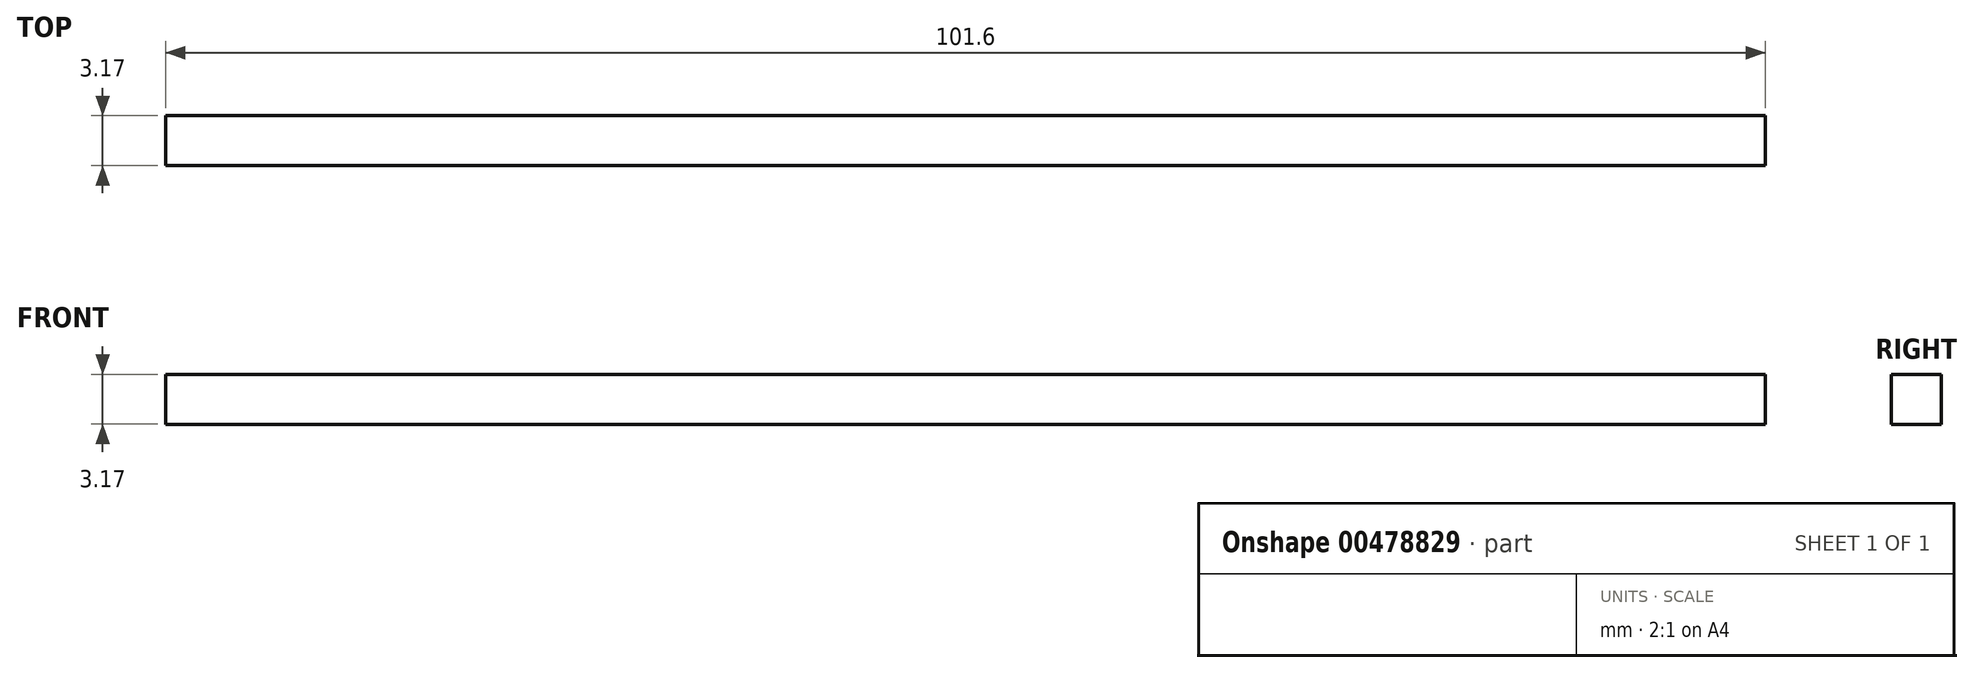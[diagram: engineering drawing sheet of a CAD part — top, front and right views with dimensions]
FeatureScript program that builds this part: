
annotation { "Feature Type Name" : "Feature", "Feature Type Description" : "" }
export const myFeature = defineFeature(function(context is Context, id is Id, definition is map)
    precondition{}
    {
        {
            var Q0;
            Q0=qCreatedBy(makeId("Front.planeOp"),FACE);
            var sketch = newSketch(context, id + "F0", { "sketchPlane" : qUnion([Q0])});
            skLineSegment(sketch, "E0.bottom", {"start": v(-96.35, 19.37) * mm, "end": v(5.25, 19.37) * mm});
            skLineSegment(sketch, "E0.top", {"start": v(-96.35, 16.2) * mm, "end": v(5.25, 16.2) * mm});
            skLineSegment(sketch, "E0.left", {"start": v(-96.35, 19.37) * mm, "end": v(-96.35, 16.2) * mm});
            skLineSegment(sketch, "E0.right", {"start": v(5.25, 19.37) * mm, "end": v(5.25, 16.2) * mm});
            skSolve(sketch);
        }
        {
            var Q0;
            Q0=makeQuery(id+"F0.imprint","IMPRINT",FACE,{"disambiguationData":[TD([[makeQuery(id+"F0.imprint","IMPRINT",EDGE,{"derivedFrom":sQuery(id+"F0.wireOp",EDGE,"E0.bottom")}),-1.0]])]});
            extrude(context, id + "F1", {"entities" : qUnion([Q0]), "depth" : 3.17 * mm});
        }
    });
